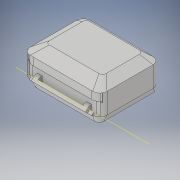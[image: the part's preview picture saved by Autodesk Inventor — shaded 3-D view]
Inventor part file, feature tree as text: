
AUTODESK INVENTOR PART (.ipt)
format: ipt  version: 2017 (Build 210142000, 142)  size: 332,800 bytes
history: native  units: in
note: dims shown in document units (in); Inventor stores cm internally (conversion verified against a paired STEP export)
features: sketch x9, extrude x8, other x6, loft x2, mirror x1
ambient origin geometry x8: Origin, YZ Plane, XZ Plane, XY Plane, X Axis, Y Axis, Z Axis, Center Point
bodies: Solid1 (feature_tree)
feature tree (26):
  extrude  "middle of body"  Depth=1.276in
  other  "top of printer"
  loft  "top part of printer"
  other  "Bottom of printer"
  loft  "bottom part of printer"
  extrude  "front bottom door slot"  Depth=0.8594in
  extrude  "front top door slot"  Depth=0.0755in
  extrude  "cords cut"  TaperAngle=0.0deg  [1 undecoded]
  extrude  "cords join curve part"  Depth=0.7135in
  other  "rack rotation Work Plane"
  extrude  "rack rotation"  Depth=0.1007in
  mirror  "Mirror of rack rotation"
  extrude  "connection to rack rotations"  TaperAngle=0.0deg  [1 undecoded]
  other  "tray work plane"
  extrude  "rest for tray"  Depth=1.3229in
  sketch  "Sketch1"  dims[d3=0.151in d4=1.276in]
  sketch  "Sketch2"  dims[d5=0.151in d6=0.8125in]
  other  "Edges1"
  other  "Edges2"
  sketch  "Sketch4"  dims[d7=0.4346in d8=0.0in d9=0.1257in]
  sketch  "Sketch5"  dims[d10=0.6016in d11=0.8594in]
  sketch  "Sketch7"  dims[d12=0.151in d13=0.0755in]
  sketch  "Sketch9"  dims[d14=0.0in d15=90.0deg d16=0.0in d17=90.0deg]
  sketch  "Sketch10"  dims[d18=0.1785in d19=0.7135in]
  sketch  "Sketch11"  dims[d21=0.0833in d22=0.1007in]
  sketch  "Sketch14"  dims[d23=0.0in d24=90.0deg d25=0.0in d26=90.0deg d27=0.3846in d30=0.3692in d31=0.1158in d32=0.0in d33=0.0833in d34=0.1158in d35=0.0in d36=0.06in d37=0.0215in d38=0.0157in d39=0.1506in d40=0.0481in d43=0.0618in d46=0.0175in d47=0.0361in d48=0.0682in d49=0.2541in d50=0.0in d57=0.0437in d62=0.0142in d63=0.0725in d64=0.0505in d65=0.1805in d66=0.0in d67=0.474in d69=0.0985in d70=0.0in d72=0.1207in d74=45.0deg d83=0.0618in d84=0.0in d85=90.0deg d87=1.3229in d88=1.3229in d89=0.0in d93=0.0289in d94=0.0618in d95=0.0589in]
note: 2 required parameter values undecoded (feature->parameter linkage not recoverable at this tier; creation-order binding heuristic only, values carry confidence <= 0.55)
